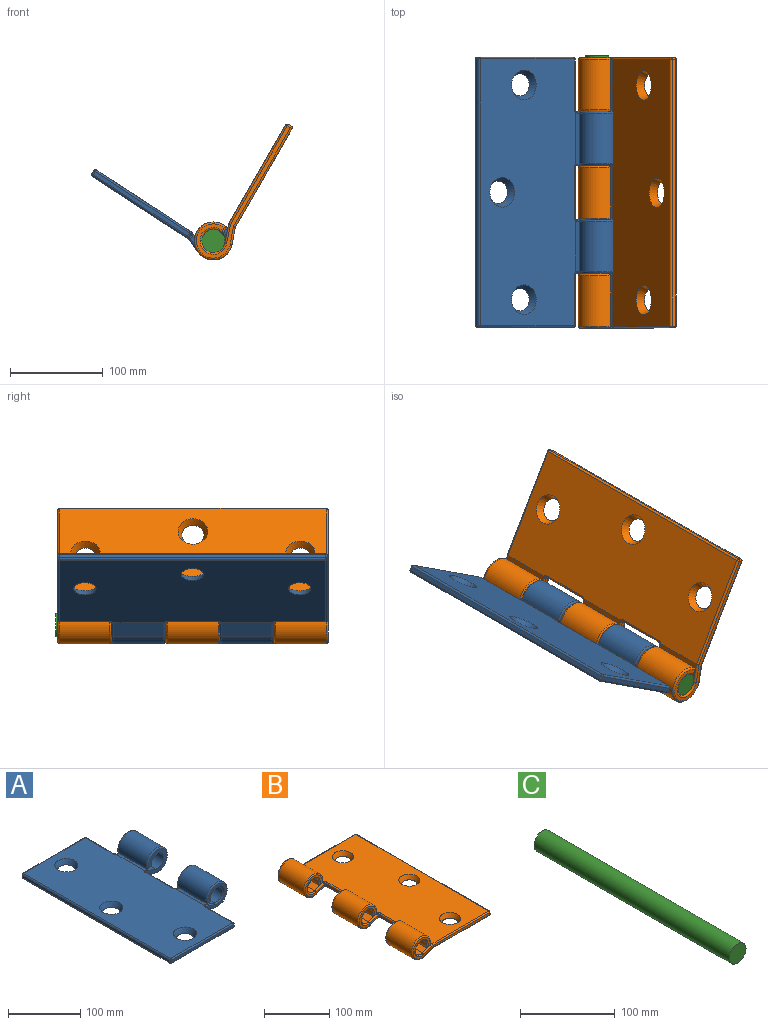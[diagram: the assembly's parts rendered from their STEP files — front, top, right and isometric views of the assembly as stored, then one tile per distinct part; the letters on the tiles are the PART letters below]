
ASSEMBLY  parts=3 mates=2
PART A: 86 faces, bbox 171.7x292x44.4 mm
  f0: cylinder r=12.5mm len=54.4mm, axis (0,1,0), area 3703.3mm2, adj f2,f8,f65,f78
  f1: cylinder r=12.5mm len=56.4mm, axis (0,1,0), area 3837.4mm2, adj f3,f9,f21,f33,f71
  f2: plane 56.21x20.54mm, normal (0.32,0,0.95), area 1179.8mm2, adj f0,f12,f66,f67,f68,f72,f74,f76
  f3: plane 57.3x20.54mm, normal (0.32,0,0.95), area 1220.4mm2, adj f1,f12,f21,f35,f37,f39,f69
  f4: plane 54.85x17.59mm, normal (-0.34,0,-0.94), area 1016.5mm2, adj f6,f14,f55,f58,f84,f85
  f5: plane 54.85x17.59mm, normal (-0.34,0,-0.94), area 1016.5mm2, adj f7,f14,f30,f32,f75,f77
  f6: cylinder r=20.5mm len=54.4mm, axis (0,1,0), area 5913.6mm2, adj f4,f8,f61,f82
  f7: cylinder r=20.5mm len=54.4mm, axis (0,1,0), area 5913.6mm2, adj f5,f9,f29,f73
  f8: plane 54.4x8.42mm, normal (0,0,-1), area 458.3mm2, adj f0,f6,f63,f80
  f9: plane 54.4x8.42mm, normal (0,0,-1), area 458.3mm2, adj f1,f7,f31,f71
  f10: plane 121x4mm, normal (0,-1,0), area 484mm2, adj f52,f53,f59,f60
  f11: plane 121x4mm, normal (0,1,0), area 484mm2, adj f40,f41,f46,f47
  f12: plane 288x123mm, normal (0,0,1), area 32665.2mm2, adj f2,f3,f15,f16,f17,f39,f42,f47
  f13: plane 288x4mm, normal (-1,0,0), area 1152mm2, adj f45,f46,f53,f54
  f14: plane 288x123.06mm, normal (0,0,-1), area 33720.8mm2, adj f4,f5,f15,f16,f17,f32,f34,f36
  f15: cone r=12mm half-angle=26.6deg, axis (0,0,1), area 786.8mm2, adj f12,f14
  f16: cone r=16mm half-angle=26.6deg, axis (0,0,1), area 786.8mm2, adj f12,f14
  f17: cone r=12mm half-angle=26.6deg, axis (0,0,1), area 786.8mm2, adj f12,f14
  f18: plane 54.4x4mm, normal (1,0,0), area 217.6mm2, adj f25,f36,f41,f42
  f19: plane 41x37mm, normal (0,1,0), area 413.9mm2, adj f25,f29,f30,f31,f33,f35
  f20: plane 54.4x4mm, normal (1,0,0), area 217.6mm2, adj f26,f27,f70,f81
  f21: plane 41.04x37.04mm, normal (0,-1,0), area 593.6mm2, adj f1,f3,f26,f69,f71,f73,f75
  f22: plane 41x37mm, normal (0,1,0), area 413.9mm2, adj f27,f76,f78,f80,f82,f84
  f23: plane 54.4x4mm, normal (1,0,0), area 217.6mm2, adj f28,f51,f59,f64
  f24: plane 41x37mm, normal (0,-1,0), area 413.9mm2, adj f28,f58,f61,f63,f65,f67
  f25: cylinder r=2mm len=4.59mm, axis (0,0,1), area 12.3mm2, adj f18,f19,f32,f34,f37,f39
  f26: cylinder r=2mm len=4.59mm, axis (0,0,-1), area 12.8mm2, adj f20,f21,f69,f77,f79
  f27: cylinder r=2mm len=4.59mm, axis (0,0,1), area 12.3mm2, adj f20,f22,f72,f74,f83,f85
  f28: cylinder r=2mm len=4.59mm, axis (0,0,-1), area 12.3mm2, adj f23,f24,f50,f55,f66,f68
  f29: torus R=18.5mm, axis (0,-1,0), area 326.9mm2, adj f7,f19,f30,f31
  f30: cylinder r=2mm len=16.94mm, axis (0.94,0,-0.34), area 54.3mm2, adj f5,f19,f29,f32
  f31: cylinder r=2mm len=8.42mm, axis (1,0,0), area 19.6mm2, adj f9,f19,f29,f33
  f32: bspline ~2.47x2.33mm, area 3.5mm2, adj f5,f14,f25,f30,f34
  f33: torus R=14.5mm, axis (0,-1,0), area 222mm2, adj f1,f19,f31,f35
  f34: torus R=4mm, axis (0,0,1), area 9.2mm2, adj f14,f25,f32,f36
  f35: cylinder r=2mm len=18.54mm, axis (-0.95,0,0.32), area 59.3mm2, adj f3,f19,f33,f37
  f36: cylinder r=2mm len=54.4mm, axis (0,-1,0), area 170.9mm2, adj f14,f18,f34,f38
  f37: bspline ~3.65x3.11mm, area 6mm2, adj f3,f25,f35,f39
  f38: sphere r=2mm, area 6.3mm2, adj f36,f40,f41
  f39: torus R=4mm, axis (0,0,-1), area 8.7mm2, adj f3,f12,f25,f37,f42
  f40: cylinder r=2mm len=121mm, axis (1,0,0), area 380.1mm2, adj f11,f14,f38,f43
  f41: cylinder r=2mm len=4mm, axis (0,0,-1), area 12.6mm2, adj f11,f18,f38,f44
  f42: cylinder r=2mm len=54.4mm, axis (0,1,0), area 170.9mm2, adj f12,f18,f39,f44
  f43: sphere r=2mm, area 6.3mm2, adj f40,f45,f46
  f44: sphere r=2mm, area 6.3mm2, adj f41,f42,f47
  f45: cylinder r=2mm len=288mm, axis (0,1,0), area 904.8mm2, adj f13,f14,f43,f48
  f46: cylinder r=2mm len=4mm, axis (0,0,-1), area 12.6mm2, adj f11,f13,f43,f49
  f47: cylinder r=2mm len=121mm, axis (-1,0,0), area 380.1mm2, adj f11,f12,f44,f49
  f48: sphere r=2mm, area 6.3mm2, adj f45,f52,f53
  f49: sphere r=2mm, area 8.6mm2, adj f46,f47,f54
  f50: torus R=4mm, axis (0,0,1), area 9.2mm2, adj f14,f28,f51,f55
  f51: cylinder r=2mm len=54.4mm, axis (0,-1,0), area 170.9mm2, adj f14,f23,f50,f56
  f52: cylinder r=2mm len=121mm, axis (-1,0,0), area 380.1mm2, adj f10,f14,f48,f56
  f53: cylinder r=2mm len=4mm, axis (0,0,1), area 12.6mm2, adj f10,f13,f48,f57
  f54: cylinder r=2mm len=288mm, axis (0,1,0), area 904.8mm2, adj f12,f13,f49,f57
  f55: bspline ~2.47x2.33mm, area 3.5mm2, adj f4,f14,f28,f50,f58
  f56: sphere r=2mm, area 6.3mm2, adj f51,f52,f59
  f57: sphere r=2mm, area 6.3mm2, adj f53,f54,f60
  f58: cylinder r=2mm len=16.94mm, axis (-0.94,0,0.34), area 54.3mm2, adj f4,f24,f55,f61
  f59: cylinder r=2mm len=4mm, axis (0,0,1), area 12.6mm2, adj f10,f23,f56,f62
  f60: cylinder r=2mm len=121mm, axis (1,0,0), area 380.1mm2, adj f10,f12,f57,f62
  f61: torus R=18.5mm, axis (0,-1,0), area 326.9mm2, adj f6,f24,f58,f63
  f62: sphere r=2mm, area 6.3mm2, adj f59,f60,f64
  f63: cylinder r=2mm len=8.42mm, axis (-1,0,0), area 19.6mm2, adj f8,f24,f61,f65
  f64: cylinder r=2mm len=54.4mm, axis (0,-1,0), area 170.9mm2, adj f12,f23,f62,f66
  f65: torus R=14.5mm, axis (0,-1,0), area 222mm2, adj f0,f24,f63,f67
  f66: torus R=4mm, axis (0,0,-1), area 8.7mm2, adj f2,f12,f28,f64,f68
  f67: cylinder r=2mm len=18.54mm, axis (0.95,0,-0.32), area 59.3mm2, adj f2,f24,f65,f68
  f68: bspline ~3.65x3.11mm, area 6mm2, adj f2,f28,f66,f67
  f69: torus R=4mm, axis (0,0,-1), area 11.9mm2, adj f3,f12,f21,f26,f70
  f70: cylinder r=2mm len=54.4mm, axis (0,1,0), area 170.9mm2, adj f12,f20,f69,f72
  f71: cylinder r=2mm len=8.42mm, axis (-1,0,0), area 22.8mm2, adj f1,f9,f21,f73
  f72: torus R=4mm, axis (0,0,-1), area 8.7mm2, adj f2,f12,f27,f70,f74
  f73: torus R=18.5mm, axis (0,-1,0), area 326.9mm2, adj f7,f21,f71,f75
  f74: bspline ~2.75x2.54mm, area 6mm2, adj f2,f27,f72,f76
  f75: cylinder r=2mm len=16.94mm, axis (-0.94,0,0.34), area 54.3mm2, adj f5,f21,f73,f77
  f76: cylinder r=2mm len=18.54mm, axis (-0.95,0,0.32), area 59.3mm2, adj f2,f22,f74,f78
  f77: bspline ~2.47x2.33mm, area 3.5mm2, adj f5,f14,f26,f75,f79
  f78: torus R=14.5mm, axis (0,-1,0), area 222mm2, adj f0,f22,f76,f80
  f79: torus R=4mm, axis (0,0,1), area 9.2mm2, adj f14,f26,f77,f81
  f80: cylinder r=2mm len=8.42mm, axis (1,0,0), area 19.6mm2, adj f8,f22,f78,f82
  f81: cylinder r=2mm len=54.4mm, axis (0,-1,0), area 170.9mm2, adj f14,f20,f79,f83
  f82: torus R=18.5mm, axis (0,-1,0), area 326.9mm2, adj f6,f22,f80,f84
  f83: torus R=4mm, axis (0,0,1), area 9.2mm2, adj f14,f27,f81,f85
  f84: cylinder r=2mm len=16.94mm, axis (0.94,0,-0.34), area 54.3mm2, adj f4,f22,f82,f85
  f85: bspline ~2.47x2.33mm, area 3.5mm2, adj f4,f14,f27,f83,f84
PART B: 95 faces, bbox 171.7x292x44.4 mm
  f0: plane 54.63x17.59mm, normal (0.34,0,-0.94), area 1016.4mm2, adj f2,f12,f42,f44,f80
  f1: plane 54.85x17.59mm, normal (0.34,0,-0.94), area 1016.5mm2, adj f3,f12,f51,f52,f62,f64
  f2: cylinder r=20.5mm len=54.4mm, axis (0,1,0), area 5913.6mm2, adj f0,f4,f40,f81
  f3: cylinder r=20.5mm len=54.4mm, axis (0,1,0), area 5913.6mm2, adj f1,f5,f49,f60
  f4: plane 54.4x8.42mm, normal (0,0,-1), area 458.3mm2, adj f2,f6,f38,f86
  f5: plane 54.4x8.42mm, normal (0,0,-1), area 458.3mm2, adj f3,f7,f47,f58
  f6: cylinder r=12.5mm len=54.4mm, axis (0,1,0), area 3703.3mm2, adj f4,f8,f36,f89
  f7: cylinder r=12.5mm len=54.4mm, axis (0,1,0), area 3703.3mm2, adj f5,f9,f45,f56
  f8: plane 55.3x20.54mm, normal (-0.32,0,0.95), area 1179mm2, adj f6,f10,f33,f34,f35,f92
  f9: plane 56.21x20.54mm, normal (-0.32,0,0.95), area 1179.8mm2, adj f7,f10,f39,f41,f43,f53,f54,f55
  f10: plane 288x123mm, normal (0,0,1), area 32774mm2, adj f8,f9,f17,f20,f21,f22,f35,f37
  f11: plane 288x4mm, normal (1,0,0), area 1152mm2, adj f83,f84,f90,f91
  f12: plane 288x123.06mm, normal (0,0,-1), area 33829.6mm2, adj f0,f1,f13,f20,f21,f22,f44,f46
  f13: plane 54.63x17.59mm, normal (0.34,0,-0.94), area 1016.4mm2, adj f12,f14,f71,f72,f75
  f14: cylinder r=20.5mm len=54.4mm, axis (0,1,0), area 5913.6mm2, adj f13,f15,f69,f73
  f15: plane 54.4x8.42mm, normal (0,0,-1), area 458.3mm2, adj f14,f16,f67,f74
  f16: cylinder r=12.5mm len=54.4mm, axis (0,1,0), area 3703.3mm2, adj f15,f17,f65,f76
  f17: plane 55.3x20.54mm, normal (-0.32,0,0.95), area 1179mm2, adj f10,f16,f59,f61,f63,f78
  f18: plane 166x37mm, normal (0,-1,0), area 913.5mm2, adj f80,f81,f85,f86,f89,f91,f92,f94
  f19: plane 166x37mm, normal (0,1,0), area 913.5mm2, adj f73,f74,f75,f76,f77,f78,f82,f83
  f20: cone r=16mm half-angle=26.6deg, axis (0,0,1), area 786.8mm2, adj f10,f12
  f21: cone r=16mm half-angle=26.6deg, axis (0,0,1), area 786.8mm2, adj f10,f12
  f22: cone r=16mm half-angle=26.6deg, axis (0,0,1), area 786.8mm2, adj f10,f12
  f23: plane 41x37mm, normal (0,1,0), area 413.9mm2, adj f29,f54,f56,f58,f60,f62
  f24: plane 54.4x4mm, normal (-1,0,0), area 217.6mm2, adj f29,f30,f57,f68
  f25: plane 41x37mm, normal (0,-1,0), area 413.9mm2, adj f30,f63,f65,f67,f69,f71
  f26: plane 41x37mm, normal (0,1,0), area 413.9mm2, adj f31,f34,f36,f38,f40,f42
  f27: plane 54.4x4mm, normal (-1,0,0), area 217.6mm2, adj f31,f32,f37,f48
  f28: plane 41x37mm, normal (0,-1,0), area 413.9mm2, adj f32,f43,f45,f47,f49,f51
  f29: cylinder r=2mm len=4.59mm, axis (0,0,1), area 12.3mm2, adj f23,f24,f53,f55,f64,f66
  f30: cylinder r=2mm len=4.59mm, axis (0,0,-1), area 12.3mm2, adj f24,f25,f59,f61,f70,f72
  f31: cylinder r=2mm len=4.59mm, axis (0,0,1), area 12.3mm2, adj f26,f27,f33,f35,f44,f46
  f32: cylinder r=2mm len=4.59mm, axis (0,0,-1), area 12.3mm2, adj f27,f28,f39,f41,f50,f52
  f33: bspline ~2.75x2.54mm, area 6mm2, adj f8,f31,f34,f35
  f34: cylinder r=2mm len=18.54mm, axis (-0.95,0,-0.32), area 59.3mm2, adj f8,f26,f33,f36
  f35: torus R=4mm, axis (0,0,-1), area 8.7mm2, adj f8,f10,f31,f33,f37
  f36: torus R=14.5mm, axis (0,1,0), area 222mm2, adj f6,f26,f34,f38
  f37: cylinder r=2mm len=54.4mm, axis (0,1,0), area 170.9mm2, adj f10,f27,f35,f39
  f38: cylinder r=2mm len=8.42mm, axis (1,0,0), area 19.6mm2, adj f4,f26,f36,f40
  f39: torus R=4mm, axis (0,0,-1), area 8.7mm2, adj f9,f10,f32,f37,f41
  f40: torus R=18.5mm, axis (0,1,0), area 326.9mm2, adj f2,f26,f38,f42
  f41: bspline ~3.65x3.11mm, area 6mm2, adj f9,f32,f39,f43
  f42: cylinder r=2mm len=16.94mm, axis (0.94,0,0.34), area 54.3mm2, adj f0,f26,f40,f44
  f43: cylinder r=2mm len=18.54mm, axis (0.95,0,0.32), area 59.3mm2, adj f9,f28,f41,f45
  f44: bspline ~2.47x2.33mm, area 3.5mm2, adj f0,f12,f31,f42,f46
  f45: torus R=14.5mm, axis (0,1,0), area 222mm2, adj f7,f28,f43,f47
  f46: torus R=4mm, axis (0,0,-1), area 9.2mm2, adj f12,f31,f44,f48
  f47: cylinder r=2mm len=8.42mm, axis (-1,0,0), area 19.6mm2, adj f5,f28,f45,f49
  f48: cylinder r=2mm len=54.4mm, axis (0,-1,0), area 170.9mm2, adj f12,f27,f46,f50
  f49: torus R=18.5mm, axis (0,1,0), area 326.9mm2, adj f3,f28,f47,f51
  f50: torus R=4mm, axis (0,0,-1), area 9.2mm2, adj f12,f32,f48,f52
  f51: cylinder r=2mm len=16.94mm, axis (-0.94,0,-0.34), area 54.3mm2, adj f1,f28,f49,f52
  f52: bspline ~2.47x2.33mm, area 3.5mm2, adj f1,f12,f32,f50,f51
  f53: bspline ~2.75x2.54mm, area 6mm2, adj f9,f29,f54,f55
  f54: cylinder r=2mm len=18.54mm, axis (-0.95,0,-0.32), area 59.3mm2, adj f9,f23,f53,f56
  f55: torus R=4mm, axis (0,0,-1), area 8.7mm2, adj f9,f10,f29,f53,f57
  f56: torus R=14.5mm, axis (0,1,0), area 222mm2, adj f7,f23,f54,f58
  f57: cylinder r=2mm len=54.4mm, axis (0,1,0), area 170.9mm2, adj f10,f24,f55,f59
  f58: cylinder r=2mm len=8.42mm, axis (1,0,0), area 19.6mm2, adj f5,f23,f56,f60
  f59: torus R=4mm, axis (0,0,-1), area 8.7mm2, adj f10,f17,f30,f57,f61
  f60: torus R=18.5mm, axis (0,1,0), area 326.9mm2, adj f3,f23,f58,f62
  f61: bspline ~3.65x3.11mm, area 6mm2, adj f17,f30,f59,f63
  f62: cylinder r=2mm len=16.94mm, axis (0.94,0,0.34), area 54.3mm2, adj f1,f23,f60,f64
  f63: cylinder r=2mm len=18.54mm, axis (0.95,0,0.32), area 59.3mm2, adj f17,f25,f61,f65
  f64: bspline ~2.47x2.33mm, area 3.5mm2, adj f1,f12,f29,f62,f66
  f65: torus R=14.5mm, axis (0,1,0), area 222mm2, adj f16,f25,f63,f67
  f66: torus R=4mm, axis (0,0,-1), area 9.2mm2, adj f12,f29,f64,f68
  f67: cylinder r=2mm len=8.42mm, axis (-1,0,0), area 19.6mm2, adj f15,f25,f65,f69
  f68: cylinder r=2mm len=54.4mm, axis (0,-1,0), area 170.9mm2, adj f12,f24,f66,f70
  f69: torus R=18.5mm, axis (0,1,0), area 326.9mm2, adj f14,f25,f67,f71
  f70: torus R=4mm, axis (0,0,-1), area 9.2mm2, adj f12,f30,f68,f72
  f71: cylinder r=2mm len=16.94mm, axis (-0.94,0,-0.34), area 54.3mm2, adj f13,f25,f69,f72
  f72: bspline ~2.47x2.33mm, area 3.5mm2, adj f12,f13,f30,f70,f71
  f73: torus R=18.5mm, axis (0,-1,0), area 326.9mm2, adj f14,f19,f74,f75
  f74: cylinder r=2mm len=8.42mm, axis (-1,0,0), area 19.6mm2, adj f15,f19,f73,f76
  f75: cylinder r=2mm len=18.59mm, axis (-0.94,0,-0.34), area 59.2mm2, adj f13,f19,f73,f77
  f76: torus R=14.5mm, axis (0,-1,0), area 222mm2, adj f16,f19,f74,f78
  f77: cylinder r=2mm len=123.35mm, axis (-1,0,0), area 387mm2, adj f12,f19,f75,f79
  f78: cylinder r=2mm len=21.18mm, axis (0.95,0,0.32), area 67.5mm2, adj f17,f19,f76,f82
  f79: sphere r=2mm, area 4mm2, adj f77,f83,f84
  f80: cylinder r=2mm len=18.59mm, axis (0.94,0,0.34), area 59.2mm2, adj f0,f18,f81,f85
  f81: torus R=18.5mm, axis (0,-1,0), area 326.9mm2, adj f2,f18,f80,f86
  f82: cylinder r=2mm len=123mm, axis (1,0,0), area 385.9mm2, adj f10,f19,f78,f87
  f83: cylinder r=2mm len=4mm, axis (0,0,-1), area 12.6mm2, adj f11,f19,f79,f87
  f84: cylinder r=2mm len=288mm, axis (0,-1,0), area 904.8mm2, adj f11,f12,f79,f88
  f85: cylinder r=2mm len=123.35mm, axis (1,0,0), area 387mm2, adj f12,f18,f80,f88
  f86: cylinder r=2mm len=8.42mm, axis (1,0,0), area 19.6mm2, adj f4,f18,f81,f89
  f87: sphere r=2mm, area 6.3mm2, adj f82,f83,f90
  f88: sphere r=2mm, area 6.3mm2, adj f84,f85,f91
  f89: torus R=14.5mm, axis (0,-1,0), area 222mm2, adj f6,f18,f86,f92
  f90: cylinder r=2mm len=288mm, axis (0,1,0), area 904.8mm2, adj f10,f11,f87,f93
  f91: cylinder r=2mm len=4mm, axis (0,0,1), area 12.6mm2, adj f11,f18,f88,f93
  f92: cylinder r=2mm len=21.18mm, axis (-0.95,0,-0.32), area 67.5mm2, adj f8,f18,f89,f94
  f93: sphere r=2mm, area 6.3mm2, adj f90,f91,f94
  f94: cylinder r=2mm len=123mm, axis (-1,0,0), area 385.9mm2, adj f10,f18,f92,f93
PART C: 3 faces, bbox 25x292x25 mm
  f0: cylinder r=12.5mm len=292mm, axis (0,-1,0), area 22933.6mm2, adj f1,f2
  f1: plane 25x25mm, normal (0,1,0), area 490.9mm2, adj f0
  f2: plane 25x25mm, normal (0,-1,0), area 490.9mm2, adj f0
PLACE A rot(axis=(0,1,0),33.2deg) t=(1.26,-1.4,14.22)mm
PLACE B rot(axis=(0,-1,0),60deg) t=(16.59,-2,-18.72)mm
PLACE C at identity fixed
MATE revolute B.f2 <-> C.f0  axis (0,-1,0) through (24.5,-292,5)mm
MATE revolute A.f0 <-> C.f0  axis (0,-1,0) through (24.5,-235,5)mm
